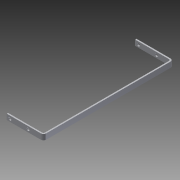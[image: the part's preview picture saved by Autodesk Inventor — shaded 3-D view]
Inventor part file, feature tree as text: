
AUTODESK INVENTOR PART (.ipt)
format: ipt  version: 2013 (Build 170138000, 138)  size: 116,736 bytes
history: native  units: in
note: dims shown in document units (in); Inventor stores cm internally (conversion verified against a paired STEP export)
features: sheet_metal_op x7, other x3, sketch x3, reference x2, extrude x1
ambient origin geometry x8: Origin, YZ Plane, XZ Plane, XY Plane, X Axis, Y Axis, Z Axis, Center Point
feature tree (16):
  sheet_metal_op  "Face2"
  sheet_metal_op  "Flange4"
  sheet_metal_op  "Flange5"
  extrude  "Extrusion2"  Depth=0.5in
  other  "Plate5"
  sketch  "Sketch6"  dims[d1=3.119in d2=0.5in]
  other  "Plate6"
  sheet_metal_op  "Bend4"
  sheet_metal_op  "Corner4"
  sketch  "Sketch7"  dims[d5=0.295in]
  other  "Plate7"
  sheet_metal_op  "Bend5"
  sheet_metal_op  "Corner5"
  sketch  "Sketch8"  dims[d8=0.125in d42=0.125in d43=0.125in d44=0.0625in d45=0.25in d46=0.125in d47=11.643in d48=90.0deg d49=0.125in d50=0.5in d51=0.125in d52=0.125in d53=0.125in d54=0.0625in d55=0.25in d56=0.125in d57=3.369in d58=90.0deg d59=0.125in d60=0.5in d61=0.125in d62=0.125in d63=99999.0in d64=0.0in]
  reference  "Reference1"
  reference  "Reference2"
